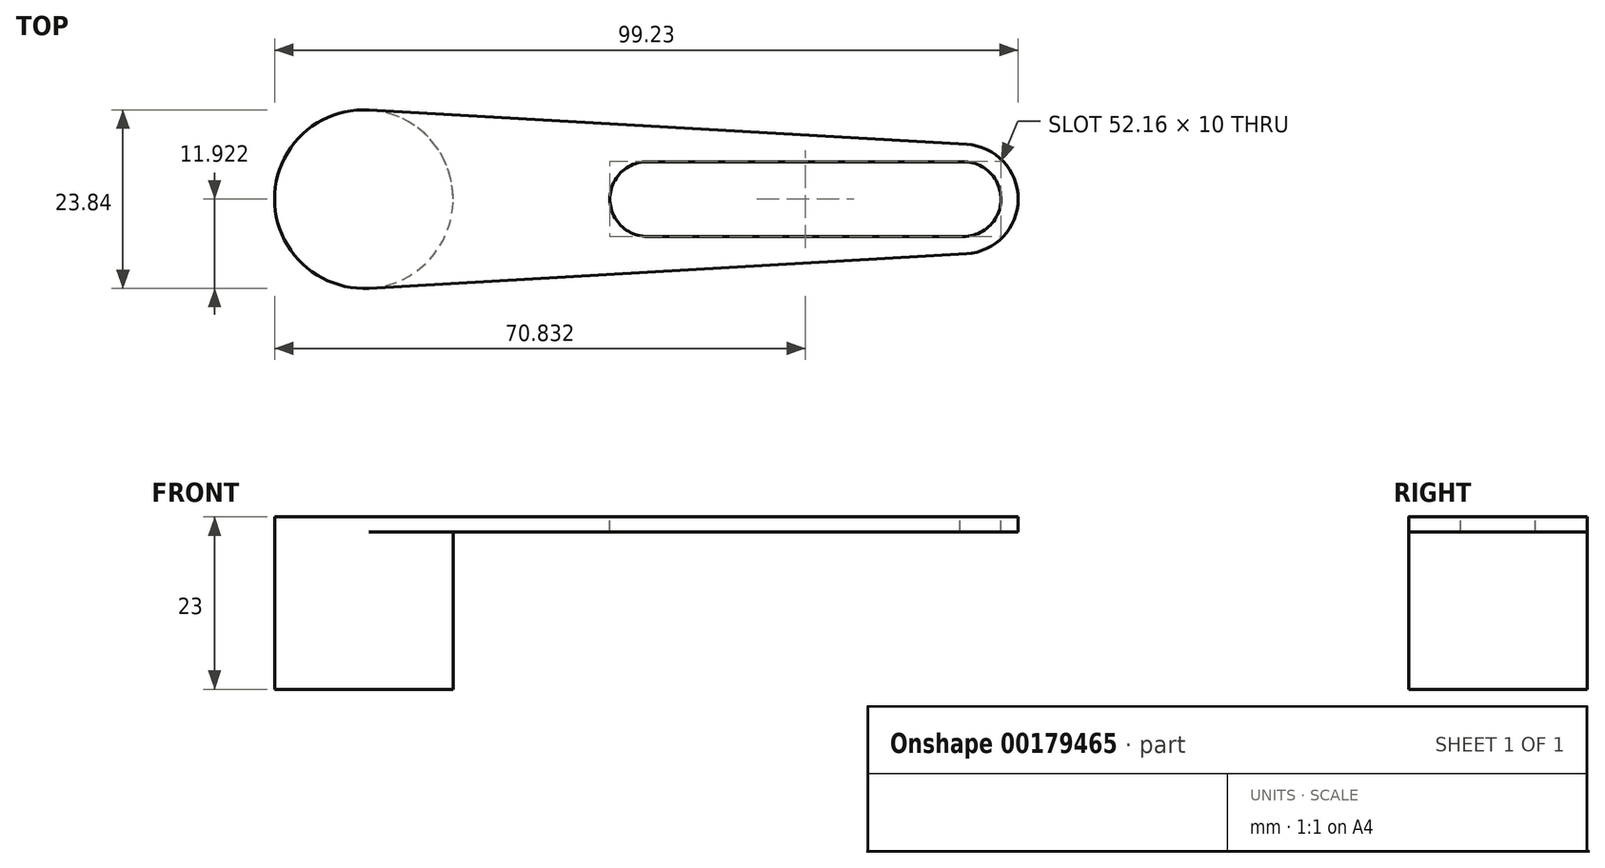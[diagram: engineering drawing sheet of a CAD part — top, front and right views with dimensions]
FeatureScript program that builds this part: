
annotation { "Feature Type Name" : "Feature", "Feature Type Description" : "" }
export const myFeature = defineFeature(function(context is Context, id is Id, definition is map)
    precondition{}
    {
        {
            var Q0;
            Q0=qCreatedBy(makeId("Top.planeOp"),FACE);
            var sketch = newSketch(context, id + "F0", { "sketchPlane" : qUnion([Q0])});
            skCircle(sketch, "E0", {"center": v(-8.94, 13.84) * mm, "radius": 11.92 * mm});
            skSolve(sketch);
        }
        {
            var Q0;
            Q0=makeQuery(id+"F0.imprint","IMPRINT",FACE,{"disambiguationData":[TD([[makeQuery(id+"F0.imprint","IMPRINT",EDGE,{"derivedFrom":sQuery(id+"F0.wireOp",EDGE,"E0")}),1.0]])]});
            extrude(context, id + "F1", {"entities" : qUnion([Q0]), "depth" : 21 * mm});
        }
        {
            var Q0;
            Q0=makeQuery(id+"F1.opExtrude","CAP_FACE",FACE,{"disambiguationData":[OSD([sQuery(id+"F0.wireOp",EDGE,"E0")])],"isStart":false});
            var sketch = newSketch(context, id + "F2", { "sketchPlane" : qUnion([Q0])});
            skLineSegment(sketch, "E1", {"start": v(-8.94, 13.84) * mm, "end": v(71.06, 13.84) * mm});
            skCircle(sketch, "E2", {"center": v(71.06, 13.84) * mm, "radius": 7.31 * mm});
            skLineSegment(sketch, "E3", {"start": v(-8.26, 25.74) * mm, "end": v(71.48, 21.14) * mm});
            skLineSegment(sketch, "E4", {"start": v(-8.26, 1.94) * mm, "end": v(71.48, 6.54) * mm});
            skSolve(sketch);
        }
        {
            var Q0;
            {var subQ0=makeQuery(id+"F1.opExtrude","CAP_EDGE",EDGE,{"disambiguationData":[OSD([sQuery(id+"F0.wireOp",EDGE,"E0")])],"isStart":false});var subQ1=makeQuery(id+"F2.imprint","INTERSECT",VERTEX,{"derivedFrom":[subQ0,sQuery(id+"F2.wireOp",EDGE,"E3")]});Q0=makeQuery(id+"F2.imprint","IMPRINT",FACE,{"disambiguationData":[TD([[makeQuery(id+"F2.imprint","IMPRINT",EDGE,{"disambiguationData":[TD([[subQ1,-1.0]])],"derivedFrom":subQ0}),1.0]])]});}
            var Q1;
            {var subQ5=sQuery(id+"F2.wireOp",EDGE,"E3");Q1=makeQuery(id+"F2.imprint","IMPRINT",FACE,{"disambiguationData":[TD([[makeQuery(id+"F2.imprint","IMPRINT",EDGE,{"derivedFrom":subQ5}),-1.0]])]});}
            var Q2;
            {var subQ5=sQuery(id+"F2.wireOp",EDGE,"E4");Q2=makeQuery(id+"F2.imprint","IMPRINT",FACE,{"disambiguationData":[TD([[makeQuery(id+"F2.imprint","IMPRINT",EDGE,{"derivedFrom":subQ5}),1.0]])]});}
            var Q3;
            {var subQ0=sQuery(id+"F2.wireOp",EDGE,"E2");var subQ1=makeQuery(id+"F2.imprint","INTERSECT",VERTEX,{"derivedFrom":[subQ0,sQuery(id+"F2.wireOp",EDGE,"E3")]});Q3=makeQuery(id+"F2.imprint","IMPRINT",FACE,{"disambiguationData":[TD([[makeQuery(id+"F2.imprint","IMPRINT",EDGE,{"disambiguationData":[TD([[subQ1,-1.0]])],"derivedFrom":subQ0}),1.0]])]});}
            extrude(context, id + "F3", {"entities" : qUnion([Q0, Q1, Q2, Q3]), "operationType" : NewBodyOperationType.ADD, "depth" : 2 * mm});
        }
        {
            var Q0;
            Q0=makeQuery(id+"F3.opExtrude","CAP_FACE",FACE,{"disambiguationData":[OSD([sQuery(id+"F0.wireOp",EDGE,"E0"),sQuery(id+"F2.wireOp",EDGE,"E2"),sQuery(id+"F2.wireOp",EDGE,"E3"),sQuery(id+"F2.wireOp",EDGE,"E4")])],"isStart":false});
            var sketch = newSketch(context, id + "F4", { "sketchPlane" : qUnion([Q0])});
            skArc(sketch, "E5", {"start": v(71.06, 8.84) * mm, "mid": v(76.05, 14.07) * mm, "end": v(70.6, 18.82) * mm});
            skArc(sketch, "E6", {"start": v(28.9, 18.84) * mm, "mid": v(23.9, 13.84) * mm, "end": v(28.9, 8.84) * mm});
            skLineSegment(sketch, "E7", {"start": v(28.9, 8.84) * mm, "end": v(71.06, 8.84) * mm});
            skLineSegment(sketch, "E8", {"start": v(28.9, 18.84) * mm, "end": v(70.6, 18.82) * mm});
            skSolve(sketch);
        }
        {
            var Q0;
            {var subQ0=sQuery(id+"F4.wireOp",EDGE,"E7");Q0=makeQuery(id+"F4.imprint","IMPRINT",FACE,{"disambiguationData":[TD([[makeQuery(id+"F4.imprint","IMPRINT",EDGE,{"derivedFrom":subQ0}),1.0]])]});}
            extrude(context, id + "F5", {"entities" : qUnion([Q0]), "operationType" : NewBodyOperationType.REMOVE, "oppositeDirection" : true, "depth" : 25 * mm});
        }
    });
